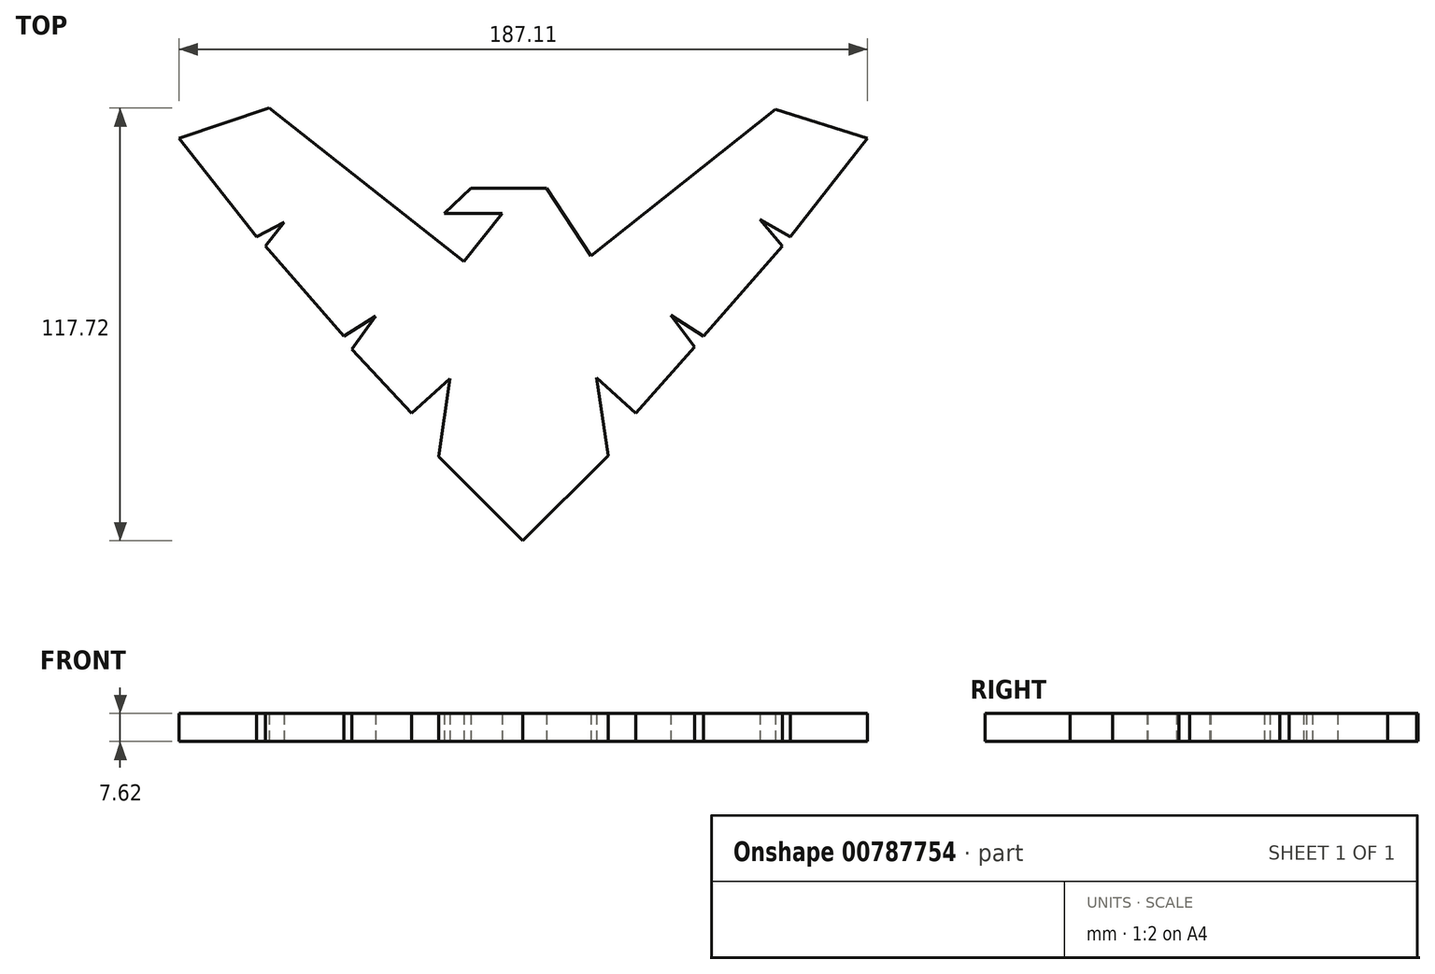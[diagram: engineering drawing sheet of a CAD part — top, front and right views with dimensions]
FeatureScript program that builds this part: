
annotation { "Feature Type Name" : "Feature", "Feature Type Description" : "" }
export const myFeature = defineFeature(function(context is Context, id is Id, definition is map)
    precondition{}
    {
        {
            var Q0;
            Q0=qCreatedBy(makeId("Top.planeOp"),FACE);
            var sketch = newSketch(context, id + "F0", { "sketchPlane" : qUnion([Q0])});
            skLineSegment(sketch, "E0", {"start": v(-14.17, 38.44) * mm, "end": v(6.42, 38.44) * mm});
            skLineSegment(sketch, "E1", {"start": v(6.42, 38.44) * mm, "end": v(18.55, 20.03) * mm});
            skLineSegment(sketch, "E2", {"start": v(18.55, 20.03) * mm, "end": v(68.72, 59.9) * mm});
            skLineSegment(sketch, "E3", {"start": v(68.72, 59.9) * mm, "end": v(93.67, 51.98) * mm});
            skLineSegment(sketch, "E4", {"start": v(93.67, 51.98) * mm, "end": v(72.79, 25.24) * mm});
            skLineSegment(sketch, "E5", {"start": v(72.79, 25.24) * mm, "end": v(64.5, 29.9) * mm});
            skLineSegment(sketch, "E6", {"start": v(64.5, 29.9) * mm, "end": v(70.59, 22.65) * mm});
            skLineSegment(sketch, "E7", {"start": v(70.59, 22.65) * mm, "end": v(49.08, -1.84) * mm});
            skLineSegment(sketch, "E8", {"start": v(49.08, -1.84) * mm, "end": v(40.23, 3.88) * mm});
            skLineSegment(sketch, "E9", {"start": v(40.23, 3.88) * mm, "end": v(46.7, -4.8) * mm});
            skLineSegment(sketch, "E10", {"start": v(46.7, -4.8) * mm, "end": v(30.72, -22.77) * mm});
            skLineSegment(sketch, "E11", {"start": v(30.72, -22.77) * mm, "end": v(20, -13.22) * mm});
            skLineSegment(sketch, "E12", {"start": v(20, -13.22) * mm, "end": v(23.2, -34.38) * mm});
            skLineSegment(sketch, "E13", {"start": v(23.2, -34.38) * mm, "end": v(0, -57.53) * mm});
            skLineSegment(sketch, "E14", {"start": v(0, -57.53) * mm, "end": v(-22.83, -34.65) * mm});
            skLineSegment(sketch, "E15", {"start": v(-22.83, -34.65) * mm, "end": v(-19.77, -13.42) * mm});
            skLineSegment(sketch, "E16", {"start": v(-19.77, -13.42) * mm, "end": v(-30.27, -22.77) * mm});
            skLineSegment(sketch, "E17", {"start": v(-30.27, -22.77) * mm, "end": v(-46.47, -5.46) * mm});
            skLineSegment(sketch, "E18", {"start": v(-46.47, -5.46) * mm, "end": v(-40.06, 3.58) * mm});
            skLineSegment(sketch, "E19", {"start": v(-40.06, 3.58) * mm, "end": v(-48.67, -1.87) * mm});
            skLineSegment(sketch, "E20", {"start": v(-48.67, -1.87) * mm, "end": v(-70.05, 22.65) * mm});
            skLineSegment(sketch, "E21", {"start": v(-70.05, 22.65) * mm, "end": v(-64.86, 29.13) * mm});
            skLineSegment(sketch, "E22", {"start": v(-64.86, 29.13) * mm, "end": v(-72.38, 25.24) * mm});
            skLineSegment(sketch, "E23", {"start": v(-72.38, 25.24) * mm, "end": v(-93.44, 51.98) * mm});
            skLineSegment(sketch, "E24", {"start": v(-93.44, 51.98) * mm, "end": v(-68.93, 60.2) * mm});
            skLineSegment(sketch, "E25", {"start": v(-68.93, 60.2) * mm, "end": v(-15.98, 18.46) * mm});
            skLineSegment(sketch, "E26", {"start": v(-15.98, 18.46) * mm, "end": v(-5.64, 31.58) * mm});
            skLineSegment(sketch, "E27", {"start": v(-5.64, 31.58) * mm, "end": v(-21.4, 31.58) * mm});
            skLineSegment(sketch, "E28", {"start": v(-21.4, 31.58) * mm, "end": v(-14.17, 38.44) * mm});
            skSolve(sketch);
        }
        {
            var Q0;
            Q0 = qSketchRegion(id + "F0", true);
            extrude(context, id + "F1", {"entities" : qUnion([Q0]), "depth" : 7.62 * mm, "offsetDistance" : 25.4 * mm});
        }
    });
